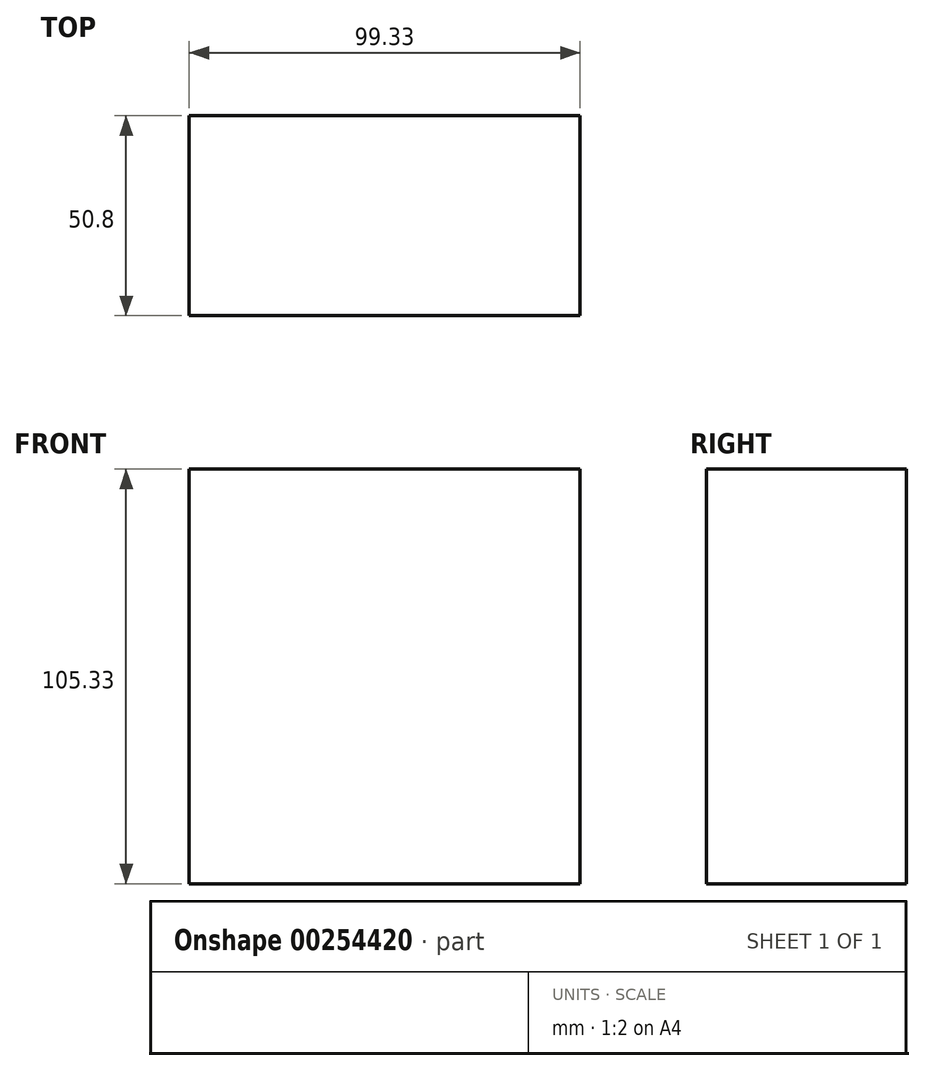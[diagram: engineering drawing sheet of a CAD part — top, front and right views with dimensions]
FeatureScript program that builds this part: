
annotation { "Feature Type Name" : "Feature", "Feature Type Description" : "" }
export const myFeature = defineFeature(function(context is Context, id is Id, definition is map)
    precondition{}
    {
        {
            var Q0;
            Q0=qCreatedBy(makeId("Front.planeOp"),FACE);
            var sketch = newSketch(context, id + "F0", { "sketchPlane" : qUnion([Q0])});
            skLineSegment(sketch, "E0.bottom", {"start": v(-51.97, 51.59) * mm, "end": v(47.36, 51.59) * mm});
            skLineSegment(sketch, "E0.top", {"start": v(-51.97, -53.74) * mm, "end": v(47.36, -53.74) * mm});
            skLineSegment(sketch, "E0.left", {"start": v(-51.97, 51.59) * mm, "end": v(-51.97, -53.74) * mm});
            skLineSegment(sketch, "E0.right", {"start": v(47.36, 51.59) * mm, "end": v(47.36, -53.74) * mm});
            skSolve(sketch);
        }
        {
            var Q0;
            Q0 = qSketchRegion(id + "F0", true);
            extrude(context, id + "F1", {"entities" : qUnion([Q0]), "depth" : 50.8 * mm});
        }
    });
